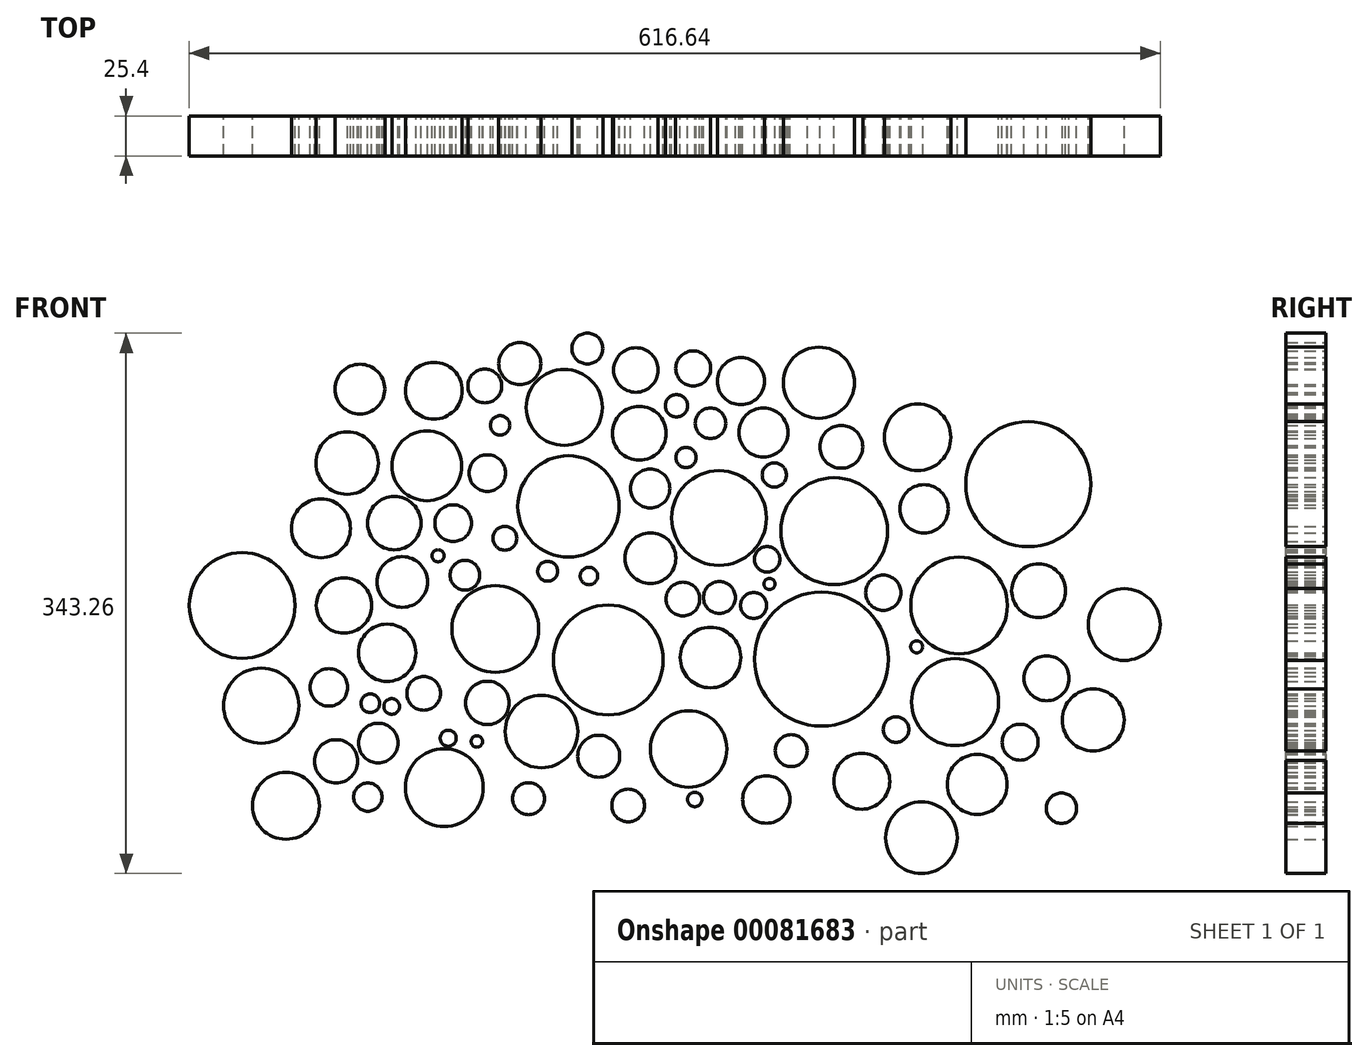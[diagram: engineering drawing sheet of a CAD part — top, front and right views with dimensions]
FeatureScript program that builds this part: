
annotation { "Feature Type Name" : "Feature", "Feature Type Description" : "" }
export const myFeature = defineFeature(function(context is Context, id is Id, definition is map)
    precondition{}
    {
        {
            var Q0;
            Q0=qCreatedBy(makeId("Front.planeOp"),FACE);
            var sketch = newSketch(context, id + "F0", { "sketchPlane" : qUnion([Q0])});
            skCircle(sketch, "E0", {"center": v(-90.18, 62.9) * mm, "radius": 32.22 * mm});
            skCircle(sketch, "E1", {"center": v(5.42, 55.53) * mm, "radius": 30.08 * mm});
            skPoint(sketch, "E1.first.point", {"position": v(-24, 49.25) * mm});
            skPoint(sketch, "E1.second.point", {"position": v(20.46, 81.58) * mm});
            skPoint(sketch, "E1.third.point", {"position": v(0, 85.12) * mm});
            skCircle(sketch, "E2", {"center": v(-136.65, -14.9) * mm, "radius": 27.56 * mm});
            skCircle(sketch, "E3", {"center": v(-64.92, -34.6) * mm, "radius": 34.87 * mm});
            skCircle(sketch, "E4", {"center": v(70.47, -34.1) * mm, "radius": 42.55 * mm});
            skCircle(sketch, "E5", {"center": v(0, -33.1) * mm, "radius": 19.21 * mm});
            skCircle(sketch, "E6", {"center": v(78.56, 47.23) * mm, "radius": 33.9 * mm});
            skCircle(sketch, "E7", {"center": v(-45.21, 109.37) * mm, "radius": 17.1 * mm});
            skCircle(sketch, "E8", {"center": v(33.6, 109.88) * mm, "radius": 15.6 * mm});
            skCircle(sketch, "E9", {"center": v(83.1, 100.78) * mm, "radius": 13.6 * mm});
            skCircle(sketch, "E10", {"center": v(135.64, 61.38) * mm, "radius": 15.36 * mm});
            skCircle(sketch, "E11", {"center": v(157.87, 0) * mm, "radius": 30.7 * mm});
            skCircle(sketch, "E12", {"center": v(155.34, -61.38) * mm, "radius": 27.64 * mm});
            skCircle(sketch, "E13", {"center": v(131.6, 106.84) * mm, "radius": 21.08 * mm});
            skCircle(sketch, "E14", {"center": v(-13.9, -91.19) * mm, "radius": 24.25 * mm});
            skCircle(sketch, "E15", {"center": v(51.28, -92.2) * mm, "radius": 10.17 * mm});
            skCircle(sketch, "E16", {"center": v(201.82, 77.04) * mm, "radius": 39.68 * mm});
            skCircle(sketch, "E17", {"center": v(-130.6, 42.69) * mm, "radius": 7.6 * mm});
            skCircle(sketch, "E18", {"center": v(-38.14, 30.06) * mm, "radius": 16.12 * mm});
            skCircle(sketch, "E19", {"center": v(-141.7, -61.89) * mm, "radius": 13.79 * mm});
            skCircle(sketch, "E20", {"center": v(-107.35, -80.07) * mm, "radius": 23.06 * mm});
            skCircle(sketch, "E21", {"center": v(-70.98, -95.74) * mm, "radius": 13.35 * mm});
            skCircle(sketch, "E22", {"center": v(-52.29, -127.06) * mm, "radius": 10.41 * mm});
            skCircle(sketch, "E23", {"center": v(-200.81, 52.28) * mm, "radius": 16.94 * mm});
            skCircle(sketch, "E24", {"center": v(-180.1, 88.66) * mm, "radius": 22.16 * mm});
            skCircle(sketch, "E25", {"center": v(-133.62, 114.42) * mm, "radius": 6.17 * mm});
            skCircle(sketch, "E26", {"center": v(-141.7, 84.11) * mm, "radius": 11.62 * mm});
            skCircle(sketch, "E27", {"center": v(-163.43, 52.28) * mm, "radius": 11.63 * mm});
            skCircle(sketch, "E28", {"center": v(-173.03, 31.57) * mm, "radius": 3.85 * mm});
            skCircle(sketch, "E29", {"center": v(-195.76, 14.9) * mm, "radius": 16.08 * mm});
            skCircle(sketch, "E30", {"center": v(-205.36, -30.06) * mm, "radius": 18.21 * mm});
            skCircle(sketch, "E31", {"center": v(-182.12, -55.83) * mm, "radius": 10.72 * mm});
            skCircle(sketch, "E32", {"center": v(208.39, 9.34) * mm, "radius": 17.1 * mm});
            skCircle(sketch, "E33", {"center": v(213.44, -46.23) * mm, "radius": 14.29 * mm});
            skCircle(sketch, "E34", {"center": v(96.11, -111.62) * mm, "radius": 17.8 * mm});
            skCircle(sketch, "E35", {"center": v(169.36, -113.64) * mm, "radius": 19.02 * mm});
            skCircle(sketch, "E36", {"center": v(35.49, -123.24) * mm, "radius": 15.07 * mm});
            skCircle(sketch, "E37", {"center": v(-169.11, -115.67) * mm, "radius": 24.7 * mm});
            skCircle(sketch, "E38", {"center": v(-211.04, -87.38) * mm, "radius": 12.55 * mm});
            skCircle(sketch, "E39", {"center": v(-232.77, 0) * mm, "radius": 17.6 * mm});
            skCircle(sketch, "E40", {"center": v(222.91, -128.8) * mm, "radius": 9.65 * mm});
            skCircle(sketch, "E41", {"center": v(243.12, -72.72) * mm, "radius": 19.7 * mm});
            skCircle(sketch, "E42", {"center": v(196.64, -86.87) * mm, "radius": 11.43 * mm});
            skCircle(sketch, "E43", {"center": v(262.82, -12.1) * mm, "radius": 22.8 * mm});
            skCircle(sketch, "E44", {"center": v(-230.75, 90.45) * mm, "radius": 19.85 * mm});
            skCircle(sketch, "E45", {"center": v(-247.42, 49.02) * mm, "radius": 18.75 * mm});
            skCircle(sketch, "E46", {"center": v(-242.36, -52.01) * mm, "radius": 11.9 * mm});
            skCircle(sketch, "E47", {"center": v(-237.82, -99) * mm, "radius": 13.74 * mm});
            skCircle(sketch, "E48", {"center": v(-217.61, -121.73) * mm, "radius": 9 * mm});
            skCircle(sketch, "E49", {"center": v(-103.44, 21.74) * mm, "radius": 6.33 * mm});
            skCircle(sketch, "E50", {"center": v(-77.17, 18.71) * mm, "radius": 5.56 * mm});
            skCircle(sketch, "E51", {"center": v(-92.83, 125.81) * mm, "radius": 24.18 * mm});
            skCircle(sketch, "E52", {"center": v(0, 115.7) * mm, "radius": 9.7 * mm});
            skCircle(sketch, "E53", {"center": v(68.83, 141.47) * mm, "radius": 22.6 * mm});
            skCircle(sketch, "E54", {"center": v(-47.36, 149.56) * mm, "radius": 14.15 * mm});
            skCircle(sketch, "E55", {"center": v(-175.68, 136.42) * mm, "radius": 18.05 * mm});
            skCircle(sketch, "E56", {"center": v(-222.66, 137.43) * mm, "radius": 15.82 * mm});
            skCircle(sketch, "E57", {"center": v(-17.56, 4.06) * mm, "radius": 10.72 * mm});
            skCircle(sketch, "E58", {"center": v(27.4, 0) * mm, "radius": 8.24 * mm});
            skCircle(sketch, "E59", {"center": v(5.68, 5.07) * mm, "radius": 10.15 * mm});
            skCircle(sketch, "E60", {"center": v(-115.56, -122.74) * mm, "radius": 10.15 * mm});
            skCircle(sketch, "E61", {"center": v(-148.4, -86.36) * mm, "radius": 3.64 * mm});
            skCircle(sketch, "E62", {"center": v(-166.59, -84.34) * mm, "radius": 5.08 * mm});
            skCircle(sketch, "E63", {"center": v(-202.45, -64.14) * mm, "radius": 5 * mm});
            skCircle(sketch, "E64", {"center": v(-216.1, -62.12) * mm, "radius": 5.91 * mm});
            skCircle(sketch, "E65", {"center": v(109.75, 8.1) * mm, "radius": 11.18 * mm});
            skCircle(sketch, "E66", {"center": v(130.97, -26.25) * mm, "radius": 3.85 * mm});
            skCircle(sketch, "E67", {"center": v(117.83, -78.79) * mm, "radius": 8.15 * mm});
            skCircle(sketch, "E68", {"center": v(134, -147.5) * mm, "radius": 22.76 * mm});
            skCircle(sketch, "E69", {"center": v(-297.43, 0) * mm, "radius": 33.6 * mm});
            skCircle(sketch, "E70", {"center": v(-285.3, -63.63) * mm, "radius": 23.9 * mm});
            skCircle(sketch, "E71", {"center": v(-269.64, -127.28) * mm, "radius": 21.24 * mm});
            skCircle(sketch, "E72", {"center": v(-155.98, 19.22) * mm, "radius": 9.44 * mm});
            skCircle(sketch, "E73", {"center": v(-143.35, 139.45) * mm, "radius": 10.74 * mm});
            skCircle(sketch, "E74", {"center": v(-121.12, 153.6) * mm, "radius": 13.35 * mm});
            skCircle(sketch, "E75", {"center": v(-10.99, 150.57) * mm, "radius": 11.13 * mm});
            skCircle(sketch, "E76", {"center": v(19.32, 142.48) * mm, "radius": 14.96 * mm});
            skCircle(sketch, "E77", {"center": v(-38.27, 74.28) * mm, "radius": 12.43 * mm});
            skCircle(sketch, "E78", {"center": v(-21.6, 126.82) * mm, "radius": 7.1 * mm});
            skCircle(sketch, "E79", {"center": v(-15.54, 93.99) * mm, "radius": 6.47 * mm});
            skCircle(sketch, "E80", {"center": v(40.54, 82.87) * mm, "radius": 7.7 * mm});
            skCircle(sketch, "E81", {"center": v(37.5, 13.66) * mm, "radius": 3.57 * mm});
            skCircle(sketch, "E82", {"center": v(36, 29.32) * mm, "radius": 8.08 * mm});
            skCircle(sketch, "E83", {"center": v(-9.98, -123.24) * mm, "radius": 4.57 * mm});
            skCircle(sketch, "E84", {"center": v(-78.18, 163.2) * mm, "radius": 9.8 * mm});
            skCircle(sketch, "E85", {"center": v(-302.75, 67.68) * mm, "radius": 29.07 * mm});
            skCircle(sketch, "E86", {"center": v(-279.87, 131.65) * mm, "radius": 19.9 * mm});
            skCircle(sketch, "E87", {"center": v(-245.55, 163.37) * mm, "radius": 12.87 * mm});
            skCircle(sketch, "E88", {"center": v(-265.3, 83.28) * mm, "radius": 8.39 * mm});
            skCircle(sketch, "E89", {"center": v(-281.43, 106.17) * mm, "radius": 3.79 * mm});
            skCircle(sketch, "E90", {"center": v(-254.9, 106.69) * mm, "radius": 3.16 * mm});
            skCircle(sketch, "E91", {"center": v(-248.15, 117.09) * mm, "radius": 6.24 * mm});
            skCircle(sketch, "E92", {"center": v(-201.34, 168.57) * mm, "radius": 15.6 * mm});
            skCircle(sketch, "E93", {"center": v(-418.2, 23.48) * mm, "radius": 79.95 * mm});
            skCircle(sketch, "E94", {"center": v(-336.04, -55.57) * mm, "radius": 18.39 * mm});
            skCircle(sketch, "E95", {"center": v(-366.72, -89.37) * mm, "radius": 3.03 * mm});
            skCircle(sketch, "E96", {"center": v(-353.2, -95.61) * mm, "radius": 4.29 * mm});
            skCircle(sketch, "E97", {"center": v(-323.54, -125.78) * mm, "radius": 22.98 * mm});
            skSolve(sketch);
        }
        {
            var Q0;
            Q0=makeQuery(id+"F0.imprint","IMPRINT",FACE,{"disambiguationData":[TD([[makeQuery(id+"F0.imprint","IMPRINT",EDGE,{"derivedFrom":sQuery(id+"F0.wireOp",EDGE,"E24")}),1.0]])]});
            extrude(context, id + "F1", {"entities" : qUnion([Q0]), "depth" : 25.4 * mm});
        }
        {
            var Q0;
            Q0=makeQuery(id+"F0.imprint","IMPRINT",FACE,{"disambiguationData":[TD([[makeQuery(id+"F0.imprint","IMPRINT",EDGE,{"derivedFrom":sQuery(id+"F0.wireOp",EDGE,"E25")}),1.0]])]});
            var Q1;
            Q1=makeQuery(id+"F0.imprint","IMPRINT",FACE,{"disambiguationData":[TD([[makeQuery(id+"F0.imprint","IMPRINT",EDGE,{"derivedFrom":sQuery(id+"F0.wireOp",EDGE,"E26")}),1.0]])]});
            var Q2;
            Q2=makeQuery(id+"F0.imprint","IMPRINT",FACE,{"disambiguationData":[TD([[makeQuery(id+"F0.imprint","IMPRINT",EDGE,{"derivedFrom":sQuery(id+"F0.wireOp",EDGE,"E0")}),1.0]])]});
            extrude(context, id + "F2", {"entities" : qUnion([Q0, Q1, Q2]), "depth" : 25.4 * mm});
        }
        {
            var Q0;
            Q0=makeQuery(id+"F0.imprint","IMPRINT",FACE,{"disambiguationData":[TD([[makeQuery(id+"F0.imprint","IMPRINT",EDGE,{"derivedFrom":sQuery(id+"F0.wireOp",EDGE,"E7")}),1.0]])]});
            var Q1;
            Q1=makeQuery(id+"F0.imprint","IMPRINT",FACE,{"disambiguationData":[TD([[makeQuery(id+"F0.imprint","IMPRINT",EDGE,{"derivedFrom":sQuery(id+"F0.wireOp",EDGE,"E1")}),1.0]])]});
            var Q2;
            Q2=makeQuery(id+"F0.imprint","IMPRINT",FACE,{"disambiguationData":[TD([[makeQuery(id+"F0.imprint","IMPRINT",EDGE,{"derivedFrom":sQuery(id+"F0.wireOp",EDGE,"E18")}),1.0]])]});
            var Q3;
            Q3=makeQuery(id+"F0.imprint","IMPRINT",FACE,{"disambiguationData":[TD([[makeQuery(id+"F0.imprint","IMPRINT",EDGE,{"derivedFrom":sQuery(id+"F0.wireOp",EDGE,"E2")}),1.0]])]});
            var Q4;
            Q4=makeQuery(id+"F0.imprint","IMPRINT",FACE,{"disambiguationData":[TD([[makeQuery(id+"F0.imprint","IMPRINT",EDGE,{"derivedFrom":sQuery(id+"F0.wireOp",EDGE,"E3")}),1.0]])]});
            var Q5;
            Q5=makeQuery(id+"F0.imprint","IMPRINT",FACE,{"disambiguationData":[TD([[makeQuery(id+"F0.imprint","IMPRINT",EDGE,{"derivedFrom":sQuery(id+"F0.wireOp",EDGE,"E20")}),1.0]])]});
            var Q6;
            Q6=makeQuery(id+"F0.imprint","IMPRINT",FACE,{"disambiguationData":[TD([[makeQuery(id+"F0.imprint","IMPRINT",EDGE,{"derivedFrom":sQuery(id+"F0.wireOp",EDGE,"E19")}),1.0]])]});
            var Q7;
            Q7=makeQuery(id+"F0.imprint","IMPRINT",FACE,{"disambiguationData":[TD([[makeQuery(id+"F0.imprint","IMPRINT",EDGE,{"derivedFrom":sQuery(id+"F0.wireOp",EDGE,"E31")}),1.0]])]});
            var Q8;
            Q8=makeQuery(id+"F0.imprint","IMPRINT",FACE,{"disambiguationData":[TD([[makeQuery(id+"F0.imprint","IMPRINT",EDGE,{"derivedFrom":sQuery(id+"F0.wireOp",EDGE,"E30")}),1.0]])]});
            var Q9;
            Q9=makeQuery(id+"F0.imprint","IMPRINT",FACE,{"disambiguationData":[TD([[makeQuery(id+"F0.imprint","IMPRINT",EDGE,{"derivedFrom":sQuery(id+"F0.wireOp",EDGE,"E29")}),1.0]])]});
            var Q10;
            Q10=makeQuery(id+"F0.imprint","IMPRINT",FACE,{"disambiguationData":[TD([[makeQuery(id+"F0.imprint","IMPRINT",EDGE,{"derivedFrom":sQuery(id+"F0.wireOp",EDGE,"E23")}),1.0]])]});
            var Q11;
            Q11=makeQuery(id+"F0.imprint","IMPRINT",FACE,{"disambiguationData":[TD([[makeQuery(id+"F0.imprint","IMPRINT",EDGE,{"derivedFrom":sQuery(id+"F0.wireOp",EDGE,"E28")}),1.0]])]});
            var Q12;
            Q12=makeQuery(id+"F0.imprint","IMPRINT",FACE,{"disambiguationData":[TD([[makeQuery(id+"F0.imprint","IMPRINT",EDGE,{"derivedFrom":sQuery(id+"F0.wireOp",EDGE,"E27")}),1.0]])]});
            var Q13;
            Q13=makeQuery(id+"F0.imprint","IMPRINT",FACE,{"disambiguationData":[TD([[makeQuery(id+"F0.imprint","IMPRINT",EDGE,{"derivedFrom":sQuery(id+"F0.wireOp",EDGE,"E17")}),1.0]])]});
            var Q14;
            Q14=makeQuery(id+"F0.imprint","IMPRINT",FACE,{"disambiguationData":[TD([[makeQuery(id+"F0.imprint","IMPRINT",EDGE,{"derivedFrom":sQuery(id+"F0.wireOp",EDGE,"E5")}),1.0]])]});
            var Q15;
            Q15=makeQuery(id+"F0.imprint","IMPRINT",FACE,{"disambiguationData":[TD([[makeQuery(id+"F0.imprint","IMPRINT",EDGE,{"derivedFrom":sQuery(id+"F0.wireOp",EDGE,"E14")}),1.0]])]});
            var Q16;
            Q16=makeQuery(id+"F0.imprint","IMPRINT",FACE,{"disambiguationData":[TD([[makeQuery(id+"F0.imprint","IMPRINT",EDGE,{"derivedFrom":sQuery(id+"F0.wireOp",EDGE,"E22")}),1.0]])]});
            var Q17;
            Q17=makeQuery(id+"F0.imprint","IMPRINT",FACE,{"disambiguationData":[TD([[makeQuery(id+"F0.imprint","IMPRINT",EDGE,{"derivedFrom":sQuery(id+"F0.wireOp",EDGE,"E21")}),1.0]])]});
            var Q18;
            Q18=makeQuery(id+"F0.imprint","IMPRINT",FACE,{"disambiguationData":[TD([[makeQuery(id+"F0.imprint","IMPRINT",EDGE,{"derivedFrom":sQuery(id+"F0.wireOp",EDGE,"E15")}),1.0]])]});
            var Q19;
            Q19=makeQuery(id+"F0.imprint","IMPRINT",FACE,{"disambiguationData":[TD([[makeQuery(id+"F0.imprint","IMPRINT",EDGE,{"derivedFrom":sQuery(id+"F0.wireOp",EDGE,"E4")}),1.0]])]});
            var Q20;
            Q20=makeQuery(id+"F0.imprint","IMPRINT",FACE,{"disambiguationData":[TD([[makeQuery(id+"F0.imprint","IMPRINT",EDGE,{"derivedFrom":sQuery(id+"F0.wireOp",EDGE,"E6")}),1.0]])]});
            var Q21;
            Q21=makeQuery(id+"F0.imprint","IMPRINT",FACE,{"disambiguationData":[TD([[makeQuery(id+"F0.imprint","IMPRINT",EDGE,{"derivedFrom":sQuery(id+"F0.wireOp",EDGE,"E8")}),1.0]])]});
            var Q22;
            Q22=makeQuery(id+"F0.imprint","IMPRINT",FACE,{"disambiguationData":[TD([[makeQuery(id+"F0.imprint","IMPRINT",EDGE,{"derivedFrom":sQuery(id+"F0.wireOp",EDGE,"E9")}),1.0]])]});
            var Q23;
            Q23=makeQuery(id+"F0.imprint","IMPRINT",FACE,{"disambiguationData":[TD([[makeQuery(id+"F0.imprint","IMPRINT",EDGE,{"derivedFrom":sQuery(id+"F0.wireOp",EDGE,"E13")}),1.0]])]});
            var Q24;
            Q24=makeQuery(id+"F0.imprint","IMPRINT",FACE,{"disambiguationData":[TD([[makeQuery(id+"F0.imprint","IMPRINT",EDGE,{"derivedFrom":sQuery(id+"F0.wireOp",EDGE,"E10")}),1.0]])]});
            var Q25;
            Q25=makeQuery(id+"F0.imprint","IMPRINT",FACE,{"disambiguationData":[TD([[makeQuery(id+"F0.imprint","IMPRINT",EDGE,{"derivedFrom":sQuery(id+"F0.wireOp",EDGE,"E16")}),1.0]])]});
            var Q26;
            Q26=makeQuery(id+"F0.imprint","IMPRINT",FACE,{"disambiguationData":[TD([[makeQuery(id+"F0.imprint","IMPRINT",EDGE,{"derivedFrom":sQuery(id+"F0.wireOp",EDGE,"E11")}),1.0]])]});
            var Q27;
            Q27=makeQuery(id+"F0.imprint","IMPRINT",FACE,{"disambiguationData":[TD([[makeQuery(id+"F0.imprint","IMPRINT",EDGE,{"derivedFrom":sQuery(id+"F0.wireOp",EDGE,"E32")}),1.0]])]});
            var Q28;
            Q28=makeQuery(id+"F0.imprint","IMPRINT",FACE,{"disambiguationData":[TD([[makeQuery(id+"F0.imprint","IMPRINT",EDGE,{"derivedFrom":sQuery(id+"F0.wireOp",EDGE,"E33")}),1.0]])]});
            var Q29;
            Q29=makeQuery(id+"F0.imprint","IMPRINT",FACE,{"disambiguationData":[TD([[makeQuery(id+"F0.imprint","IMPRINT",EDGE,{"derivedFrom":sQuery(id+"F0.wireOp",EDGE,"E12")}),1.0]])]});
            extrude(context, id + "F3", {"entities" : qUnion([Q0, Q1, Q2, Q3, Q4, Q5, Q6, Q7, Q8, Q9, Q10, Q11, Q12, Q13, Q14, Q15, Q16, Q17, Q18, Q19, Q20, Q21, Q22, Q23, Q24, Q25, Q26, Q27, Q28, Q29]), "depth" : 25.4 * mm});
        }
        {
            var Q0;
            Q0=makeQuery(id+"F0.imprint","IMPRINT",FACE,{"disambiguationData":[TD([[makeQuery(id+"F0.imprint","IMPRINT",EDGE,{"derivedFrom":sQuery(id+"F0.wireOp",EDGE,"E69")}),1.0]])]});
            var Q1;
            Q1=makeQuery(id+"F0.imprint","IMPRINT",FACE,{"disambiguationData":[TD([[makeQuery(id+"F0.imprint","IMPRINT",EDGE,{"derivedFrom":sQuery(id+"F0.wireOp",EDGE,"E70")}),1.0]])]});
            var Q2;
            Q2=makeQuery(id+"F0.imprint","IMPRINT",FACE,{"disambiguationData":[TD([[makeQuery(id+"F0.imprint","IMPRINT",EDGE,{"derivedFrom":sQuery(id+"F0.wireOp",EDGE,"E71")}),1.0]])]});
            var Q3;
            Q3=makeQuery(id+"F0.imprint","IMPRINT",FACE,{"disambiguationData":[TD([[makeQuery(id+"F0.imprint","IMPRINT",EDGE,{"derivedFrom":sQuery(id+"F0.wireOp",EDGE,"E48")}),1.0]])]});
            var Q4;
            Q4=makeQuery(id+"F0.imprint","IMPRINT",FACE,{"disambiguationData":[TD([[makeQuery(id+"F0.imprint","IMPRINT",EDGE,{"derivedFrom":sQuery(id+"F0.wireOp",EDGE,"E47")}),1.0]])]});
            var Q5;
            Q5=makeQuery(id+"F0.imprint","IMPRINT",FACE,{"disambiguationData":[TD([[makeQuery(id+"F0.imprint","IMPRINT",EDGE,{"derivedFrom":sQuery(id+"F0.wireOp",EDGE,"E38")}),1.0]])]});
            var Q6;
            Q6=makeQuery(id+"F0.imprint","IMPRINT",FACE,{"disambiguationData":[TD([[makeQuery(id+"F0.imprint","IMPRINT",EDGE,{"derivedFrom":sQuery(id+"F0.wireOp",EDGE,"E46")}),1.0]])]});
            var Q7;
            Q7=makeQuery(id+"F0.imprint","IMPRINT",FACE,{"disambiguationData":[TD([[makeQuery(id+"F0.imprint","IMPRINT",EDGE,{"derivedFrom":sQuery(id+"F0.wireOp",EDGE,"E64")}),1.0]])]});
            var Q8;
            Q8=makeQuery(id+"F0.imprint","IMPRINT",FACE,{"disambiguationData":[TD([[makeQuery(id+"F0.imprint","IMPRINT",EDGE,{"derivedFrom":sQuery(id+"F0.wireOp",EDGE,"E63")}),1.0]])]});
            var Q9;
            Q9=makeQuery(id+"F0.imprint","IMPRINT",FACE,{"disambiguationData":[TD([[makeQuery(id+"F0.imprint","IMPRINT",EDGE,{"derivedFrom":sQuery(id+"F0.wireOp",EDGE,"E37")}),1.0]])]});
            var Q10;
            Q10=makeQuery(id+"F0.imprint","IMPRINT",FACE,{"disambiguationData":[TD([[makeQuery(id+"F0.imprint","IMPRINT",EDGE,{"derivedFrom":sQuery(id+"F0.wireOp",EDGE,"E62")}),1.0]])]});
            var Q11;
            Q11=makeQuery(id+"F0.imprint","IMPRINT",FACE,{"disambiguationData":[TD([[makeQuery(id+"F0.imprint","IMPRINT",EDGE,{"derivedFrom":sQuery(id+"F0.wireOp",EDGE,"E61")}),1.0]])]});
            var Q12;
            Q12=makeQuery(id+"F0.imprint","IMPRINT",FACE,{"disambiguationData":[TD([[makeQuery(id+"F0.imprint","IMPRINT",EDGE,{"derivedFrom":sQuery(id+"F0.wireOp",EDGE,"E60")}),1.0]])]});
            var Q13;
            Q13=makeQuery(id+"F0.imprint","IMPRINT",FACE,{"disambiguationData":[TD([[makeQuery(id+"F0.imprint","IMPRINT",EDGE,{"derivedFrom":sQuery(id+"F0.wireOp",EDGE,"E72")}),1.0]])]});
            var Q14;
            Q14=makeQuery(id+"F0.imprint","IMPRINT",FACE,{"disambiguationData":[TD([[makeQuery(id+"F0.imprint","IMPRINT",EDGE,{"derivedFrom":sQuery(id+"F0.wireOp",EDGE,"E49")}),1.0]])]});
            var Q15;
            Q15=makeQuery(id+"F0.imprint","IMPRINT",FACE,{"disambiguationData":[TD([[makeQuery(id+"F0.imprint","IMPRINT",EDGE,{"derivedFrom":sQuery(id+"F0.wireOp",EDGE,"E50")}),1.0]])]});
            var Q16;
            Q16=makeQuery(id+"F0.imprint","IMPRINT",FACE,{"disambiguationData":[TD([[makeQuery(id+"F0.imprint","IMPRINT",EDGE,{"derivedFrom":sQuery(id+"F0.wireOp",EDGE,"E57")}),1.0]])]});
            var Q17;
            Q17=makeQuery(id+"F0.imprint","IMPRINT",FACE,{"disambiguationData":[TD([[makeQuery(id+"F0.imprint","IMPRINT",EDGE,{"derivedFrom":sQuery(id+"F0.wireOp",EDGE,"E59")}),1.0]])]});
            var Q18;
            Q18=makeQuery(id+"F0.imprint","IMPRINT",FACE,{"disambiguationData":[TD([[makeQuery(id+"F0.imprint","IMPRINT",EDGE,{"derivedFrom":sQuery(id+"F0.wireOp",EDGE,"E58")}),1.0]])]});
            var Q19;
            Q19=makeQuery(id+"F0.imprint","IMPRINT",FACE,{"disambiguationData":[TD([[makeQuery(id+"F0.imprint","IMPRINT",EDGE,{"derivedFrom":sQuery(id+"F0.wireOp",EDGE,"E81")}),1.0]])]});
            var Q20;
            Q20=makeQuery(id+"F0.imprint","IMPRINT",FACE,{"disambiguationData":[TD([[makeQuery(id+"F0.imprint","IMPRINT",EDGE,{"derivedFrom":sQuery(id+"F0.wireOp",EDGE,"E82")}),1.0]])]});
            var Q21;
            Q21=makeQuery(id+"F0.imprint","IMPRINT",FACE,{"disambiguationData":[TD([[makeQuery(id+"F0.imprint","IMPRINT",EDGE,{"derivedFrom":sQuery(id+"F0.wireOp",EDGE,"E80")}),1.0]])]});
            var Q22;
            Q22=makeQuery(id+"F0.imprint","IMPRINT",FACE,{"disambiguationData":[TD([[makeQuery(id+"F0.imprint","IMPRINT",EDGE,{"derivedFrom":sQuery(id+"F0.wireOp",EDGE,"E52")}),1.0]])]});
            var Q23;
            Q23=makeQuery(id+"F0.imprint","IMPRINT",FACE,{"disambiguationData":[TD([[makeQuery(id+"F0.imprint","IMPRINT",EDGE,{"derivedFrom":sQuery(id+"F0.wireOp",EDGE,"E79")}),1.0]])]});
            var Q24;
            Q24=makeQuery(id+"F0.imprint","IMPRINT",FACE,{"disambiguationData":[TD([[makeQuery(id+"F0.imprint","IMPRINT",EDGE,{"derivedFrom":sQuery(id+"F0.wireOp",EDGE,"E77")}),1.0]])]});
            var Q25;
            Q25=makeQuery(id+"F0.imprint","IMPRINT",FACE,{"disambiguationData":[TD([[makeQuery(id+"F0.imprint","IMPRINT",EDGE,{"derivedFrom":sQuery(id+"F0.wireOp",EDGE,"E78")}),1.0]])]});
            var Q26;
            Q26=makeQuery(id+"F0.imprint","IMPRINT",FACE,{"disambiguationData":[TD([[makeQuery(id+"F0.imprint","IMPRINT",EDGE,{"derivedFrom":sQuery(id+"F0.wireOp",EDGE,"E76")}),1.0]])]});
            var Q27;
            Q27=makeQuery(id+"F0.imprint","IMPRINT",FACE,{"disambiguationData":[TD([[makeQuery(id+"F0.imprint","IMPRINT",EDGE,{"derivedFrom":sQuery(id+"F0.wireOp",EDGE,"E53")}),1.0]])]});
            var Q28;
            Q28=makeQuery(id+"F0.imprint","IMPRINT",FACE,{"disambiguationData":[TD([[makeQuery(id+"F0.imprint","IMPRINT",EDGE,{"derivedFrom":sQuery(id+"F0.wireOp",EDGE,"E54")}),1.0]])]});
            var Q29;
            Q29=makeQuery(id+"F0.imprint","IMPRINT",FACE,{"disambiguationData":[TD([[makeQuery(id+"F0.imprint","IMPRINT",EDGE,{"derivedFrom":sQuery(id+"F0.wireOp",EDGE,"E51")}),1.0]])]});
            var Q30;
            Q30=makeQuery(id+"F0.imprint","IMPRINT",FACE,{"disambiguationData":[TD([[makeQuery(id+"F0.imprint","IMPRINT",EDGE,{"derivedFrom":sQuery(id+"F0.wireOp",EDGE,"E75")}),1.0]])]});
            var Q31;
            Q31=makeQuery(id+"F0.imprint","IMPRINT",FACE,{"disambiguationData":[TD([[makeQuery(id+"F0.imprint","IMPRINT",EDGE,{"derivedFrom":sQuery(id+"F0.wireOp",EDGE,"E84")}),1.0]])]});
            var Q32;
            Q32=makeQuery(id+"F0.imprint","IMPRINT",FACE,{"disambiguationData":[TD([[makeQuery(id+"F0.imprint","IMPRINT",EDGE,{"derivedFrom":sQuery(id+"F0.wireOp",EDGE,"E74")}),1.0]])]});
            var Q33;
            Q33=makeQuery(id+"F0.imprint","IMPRINT",FACE,{"disambiguationData":[TD([[makeQuery(id+"F0.imprint","IMPRINT",EDGE,{"derivedFrom":sQuery(id+"F0.wireOp",EDGE,"E73")}),1.0]])]});
            var Q34;
            Q34=makeQuery(id+"F0.imprint","IMPRINT",FACE,{"disambiguationData":[TD([[makeQuery(id+"F0.imprint","IMPRINT",EDGE,{"derivedFrom":sQuery(id+"F0.wireOp",EDGE,"E55")}),1.0]])]});
            var Q35;
            Q35=makeQuery(id+"F0.imprint","IMPRINT",FACE,{"disambiguationData":[TD([[makeQuery(id+"F0.imprint","IMPRINT",EDGE,{"derivedFrom":sQuery(id+"F0.wireOp",EDGE,"E56")}),1.0]])]});
            var Q36;
            Q36=makeQuery(id+"F0.imprint","IMPRINT",FACE,{"disambiguationData":[TD([[makeQuery(id+"F0.imprint","IMPRINT",EDGE,{"derivedFrom":sQuery(id+"F0.wireOp",EDGE,"E44")}),1.0]])]});
            var Q37;
            Q37=makeQuery(id+"F0.imprint","IMPRINT",FACE,{"disambiguationData":[TD([[makeQuery(id+"F0.imprint","IMPRINT",EDGE,{"derivedFrom":sQuery(id+"F0.wireOp",EDGE,"E45")}),1.0]])]});
            var Q38;
            Q38=makeQuery(id+"F0.imprint","IMPRINT",FACE,{"disambiguationData":[TD([[makeQuery(id+"F0.imprint","IMPRINT",EDGE,{"derivedFrom":sQuery(id+"F0.wireOp",EDGE,"E39")}),1.0]])]});
            var Q39;
            Q39=makeQuery(id+"F0.imprint","IMPRINT",FACE,{"disambiguationData":[TD([[makeQuery(id+"F0.imprint","IMPRINT",EDGE,{"derivedFrom":sQuery(id+"F0.wireOp",EDGE,"E83")}),1.0]])]});
            var Q40;
            Q40=makeQuery(id+"F0.imprint","IMPRINT",FACE,{"disambiguationData":[TD([[makeQuery(id+"F0.imprint","IMPRINT",EDGE,{"derivedFrom":sQuery(id+"F0.wireOp",EDGE,"E36")}),1.0]])]});
            var Q41;
            Q41=makeQuery(id+"F0.imprint","IMPRINT",FACE,{"disambiguationData":[TD([[makeQuery(id+"F0.imprint","IMPRINT",EDGE,{"derivedFrom":sQuery(id+"F0.wireOp",EDGE,"E34")}),1.0]])]});
            var Q42;
            Q42=makeQuery(id+"F0.imprint","IMPRINT",FACE,{"disambiguationData":[TD([[makeQuery(id+"F0.imprint","IMPRINT",EDGE,{"derivedFrom":sQuery(id+"F0.wireOp",EDGE,"E67")}),1.0]])]});
            var Q43;
            Q43=makeQuery(id+"F0.imprint","IMPRINT",FACE,{"disambiguationData":[TD([[makeQuery(id+"F0.imprint","IMPRINT",EDGE,{"derivedFrom":sQuery(id+"F0.wireOp",EDGE,"E68")}),1.0]])]});
            var Q44;
            Q44=makeQuery(id+"F0.imprint","IMPRINT",FACE,{"disambiguationData":[TD([[makeQuery(id+"F0.imprint","IMPRINT",EDGE,{"derivedFrom":sQuery(id+"F0.wireOp",EDGE,"E35")}),1.0]])]});
            var Q45;
            Q45=makeQuery(id+"F0.imprint","IMPRINT",FACE,{"disambiguationData":[TD([[makeQuery(id+"F0.imprint","IMPRINT",EDGE,{"derivedFrom":sQuery(id+"F0.wireOp",EDGE,"E42")}),1.0]])]});
            var Q46;
            Q46=makeQuery(id+"F0.imprint","IMPRINT",FACE,{"disambiguationData":[TD([[makeQuery(id+"F0.imprint","IMPRINT",EDGE,{"derivedFrom":sQuery(id+"F0.wireOp",EDGE,"E40")}),1.0]])]});
            var Q47;
            Q47=makeQuery(id+"F0.imprint","IMPRINT",FACE,{"disambiguationData":[TD([[makeQuery(id+"F0.imprint","IMPRINT",EDGE,{"derivedFrom":sQuery(id+"F0.wireOp",EDGE,"E41")}),1.0]])]});
            var Q48;
            Q48=makeQuery(id+"F0.imprint","IMPRINT",FACE,{"disambiguationData":[TD([[makeQuery(id+"F0.imprint","IMPRINT",EDGE,{"derivedFrom":sQuery(id+"F0.wireOp",EDGE,"E43")}),1.0]])]});
            var Q49;
            Q49=makeQuery(id+"F0.imprint","IMPRINT",FACE,{"disambiguationData":[TD([[makeQuery(id+"F0.imprint","IMPRINT",EDGE,{"derivedFrom":sQuery(id+"F0.wireOp",EDGE,"E66")}),1.0]])]});
            var Q50;
            Q50=makeQuery(id+"F0.imprint","IMPRINT",FACE,{"disambiguationData":[TD([[makeQuery(id+"F0.imprint","IMPRINT",EDGE,{"derivedFrom":sQuery(id+"F0.wireOp",EDGE,"E65")}),1.0]])]});
            extrude(context, id + "F4", {"entities" : qUnion([Q0, Q1, Q2, Q3, Q4, Q5, Q6, Q7, Q8, Q9, Q10, Q11, Q12, Q13, Q14, Q15, Q16, Q17, Q18, Q19, Q20, Q21, Q22, Q23, Q24, Q25, Q26, Q27, Q28, Q29, Q30, Q31, Q32, Q33, Q34, Q35, Q36, Q37, Q38, Q39, Q40, Q41, Q42, Q43, Q44, Q45, Q46, Q47, Q48, Q49, Q50]), "depth" : 25.4 * mm});
        }
    });
